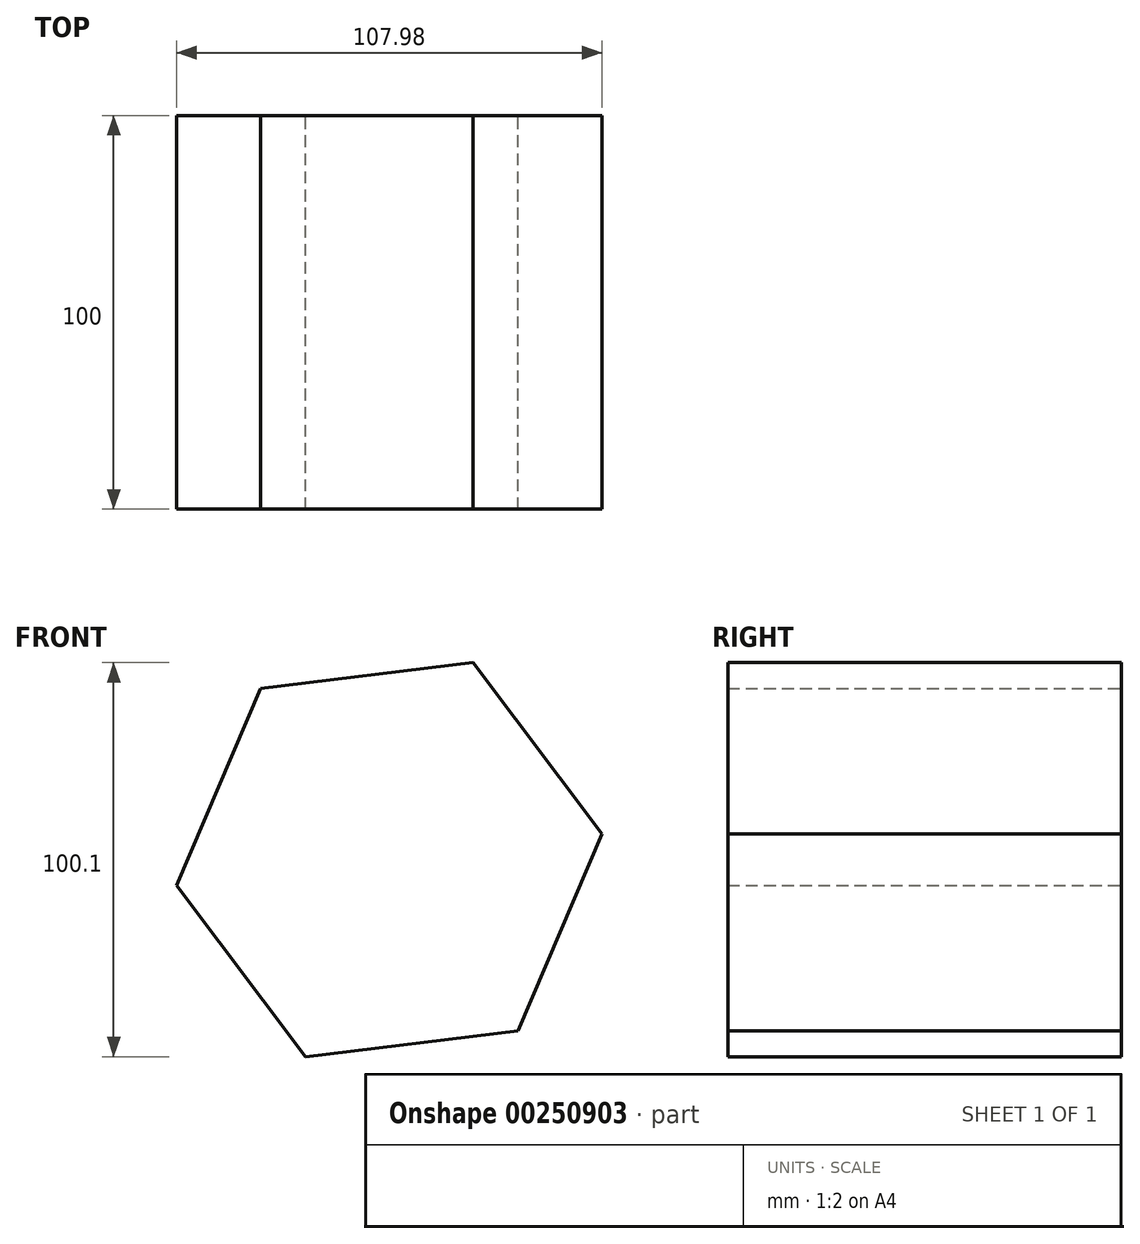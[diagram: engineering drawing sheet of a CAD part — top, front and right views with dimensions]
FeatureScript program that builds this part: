
annotation { "Feature Type Name" : "Feature", "Feature Type Description" : "" }
export const myFeature = defineFeature(function(context is Context, id is Id, definition is map)
    precondition{}
    {
        {
            var Q0;
            Q0=qCreatedBy(makeId("Front.planeOp"),FACE);
            var sketch = newSketch(context, id + "F0", { "sketchPlane" : qUnion([Q0])});
            skCircle(sketch, "E0.cCircle", {"center": v(0, 0) * mm, "radius": 54.4 * mm, "construction": true});
            skLineSegment(sketch, "E0.0", {"start": v(32.7, -43.46) * mm, "end": v(-21.29, -50.05) * mm});
            skLineSegment(sketch, "E0.1", {"start": v(-21.29, -50.05) * mm, "end": v(-54, -6.6) * mm});
            skLineSegment(sketch, "E0.2", {"start": v(-54, -6.6) * mm, "end": v(-32.7, 43.46) * mm});
            skLineSegment(sketch, "E0.3", {"start": v(-32.7, 43.46) * mm, "end": v(21.29, 50.05) * mm});
            skLineSegment(sketch, "E0.4", {"start": v(21.29, 50.05) * mm, "end": v(54, 6.6) * mm});
            skLineSegment(sketch, "E0.5", {"start": v(54, 6.6) * mm, "end": v(32.7, -43.46) * mm});
            skSolve(sketch);
        }
        {
            var Q0;
            Q0=makeQuery(id+"F0.imprint","IMPRINT",FACE,{"disambiguationData":[TD([[makeQuery(id+"F0.imprint","IMPRINT",EDGE,{"derivedFrom":sQuery(id+"F0.wireOp",EDGE,"E0.0")}),-1.0]])]});
            extrude(context, id + "F1", {"entities" : qUnion([Q0]), "depth" : 100 * mm});
        }
    });
